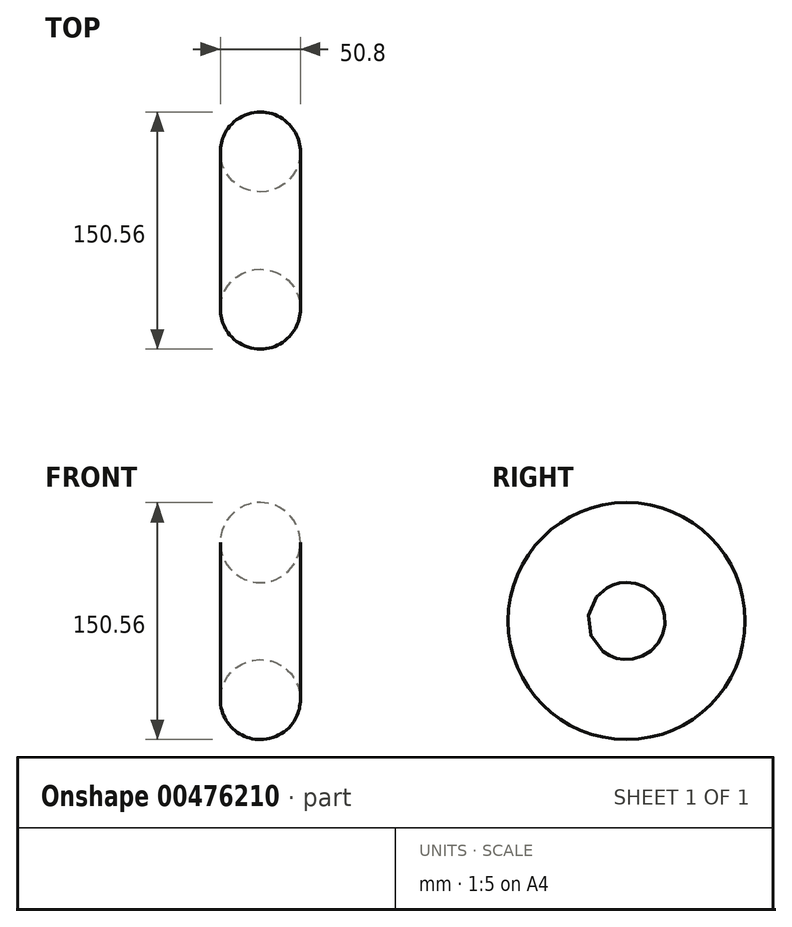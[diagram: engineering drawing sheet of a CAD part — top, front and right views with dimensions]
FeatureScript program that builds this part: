
annotation { "Feature Type Name" : "Feature", "Feature Type Description" : "" }
export const myFeature = defineFeature(function(context is Context, id is Id, definition is map)
    precondition{}
    {
        {
            var Q0;
            Q0=qCreatedBy(makeId("Front.planeOp"),FACE);
            var sketch = newSketch(context, id + "F0", { "sketchPlane" : qUnion([Q0])});
            skCircle(sketch, "E0", {"center": v(0, 0) * mm, "radius": 25.4 * mm});
            skSolve(sketch);
        }
        {
            var Q0;
            Q0=qCreatedBy(makeId("Front.planeOp"),FACE);
            var sketch = newSketch(context, id + "F1", { "sketchPlane" : qUnion([Q0])});
            skLineSegment(sketch, "E1", {"start": v(-50.5, -49.88) * mm, "end": v(101.9, -49.88) * mm});
            skSolve(sketch);
        }
        {
            var Q0;
            Q0=makeQuery(id+"F0.imprint","IMPRINT",FACE,{"disambiguationData":[TD([[makeQuery(id+"F0.imprint","IMPRINT",EDGE,{"derivedFrom":sQuery(id+"F0.wireOp",EDGE,"E0")}),1.0]])]});
            var Q1;
            Q1=sQuery(id+"F1.wireOp",EDGE,"E1");
            revolve(context, id + "F2", {"entities" : qUnion([Q0]), "axis" : qUnion([Q1]), "revolveType" : RevolveType.FULL});
        }
    });
